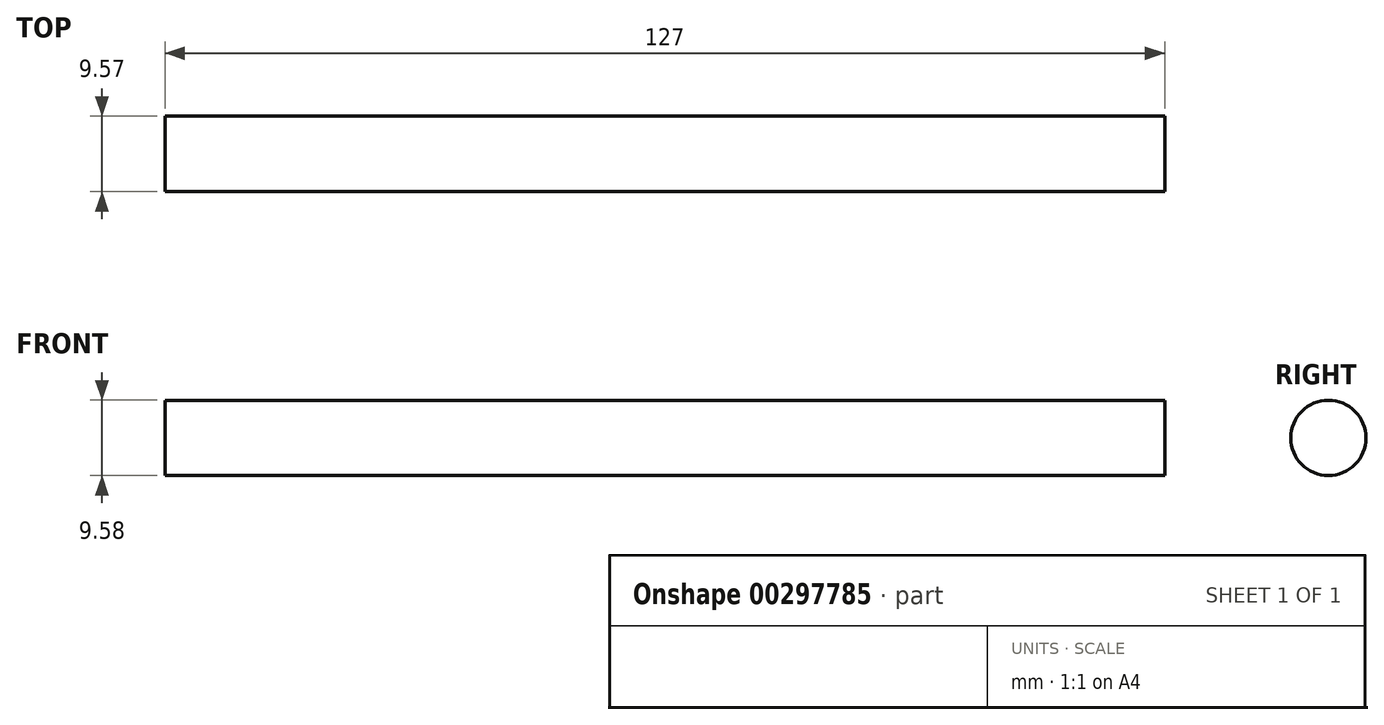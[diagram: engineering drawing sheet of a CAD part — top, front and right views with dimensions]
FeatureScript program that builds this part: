
annotation { "Feature Type Name" : "Feature", "Feature Type Description" : "" }
export const myFeature = defineFeature(function(context is Context, id is Id, definition is map)
    precondition{}
    {
        {
            var Q0;
            Q0=qCreatedBy(makeId("Right.planeOp"),FACE);
            var sketch = newSketch(context, id + "F0", { "sketchPlane" : qUnion([Q0])});
            skCircle(sketch, "E0", {"center": v(-5.05, 10.95) * mm, "radius": 4.79 * mm});
            skSolve(sketch);
        }
        {
            var Q0;
            Q0=makeQuery(id+"F0.imprint","IMPRINT",FACE,{"disambiguationData":[TD([[makeQuery(id+"F0.imprint","IMPRINT",EDGE,{"derivedFrom":sQuery(id+"F0.wireOp",EDGE,"E0")}),1.0]])]});
            extrude(context, id + "F1", {"entities" : qUnion([Q0]), "depth" : 127 * mm});
        }
    });
